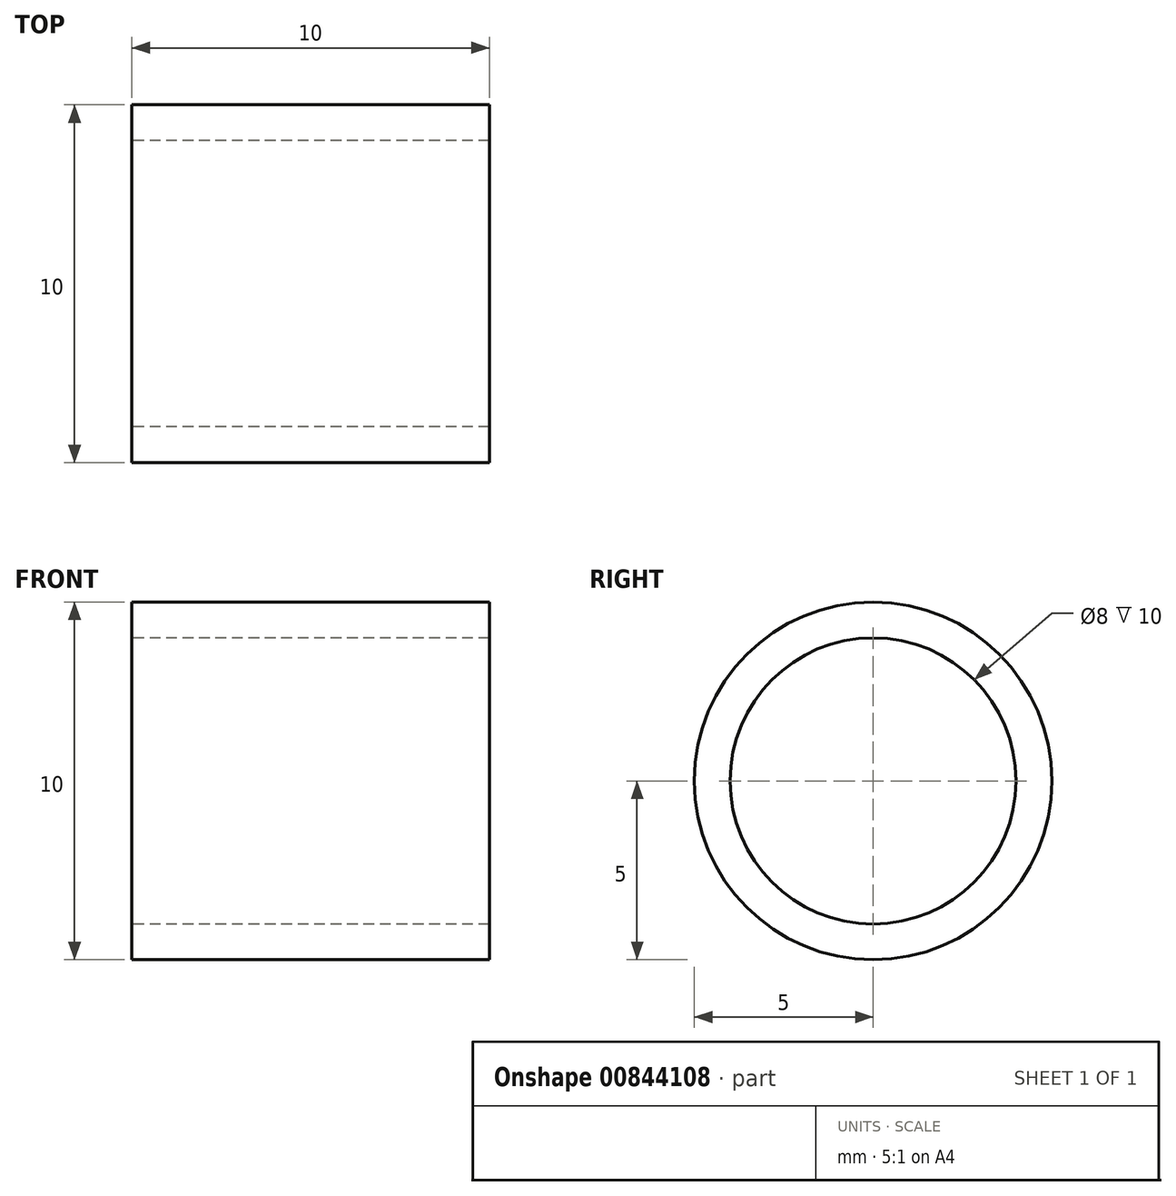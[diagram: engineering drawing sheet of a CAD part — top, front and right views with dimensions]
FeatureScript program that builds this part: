
annotation { "Feature Type Name" : "Feature", "Feature Type Description" : "" }
export const myFeature = defineFeature(function(context is Context, id is Id, definition is map)
    precondition{}
    {
        {
            var Q0;
            Q0=qCreatedBy(makeId("Right.planeOp"),FACE);
            var sketch = newSketch(context, id + "F0", { "sketchPlane" : qUnion([Q0])});
            skCircle(sketch, "E0", {"center": v(0, 0) * mm, "radius": 4 * mm});
            skCircle(sketch, "E1", {"center": v(0, 0) * mm, "radius": 5 * mm});
            skSolve(sketch);
        }
        {
            var Q0;
            Q0=makeQuery(id+"F0.imprint","IMPRINT",FACE,{"disambiguationData":[TD([[makeQuery(id+"F0.imprint","IMPRINT",EDGE,{"derivedFrom":sQuery(id+"F0.wireOp",EDGE,"E0")}),-1.0]])]});
            extrude(context, id + "F1", {"entities" : qUnion([Q0]), "endBound" : BoundingType.SYMMETRIC, "depth" : 10 * mm, "offsetDistance" : 25.4 * mm});
        }
    });
